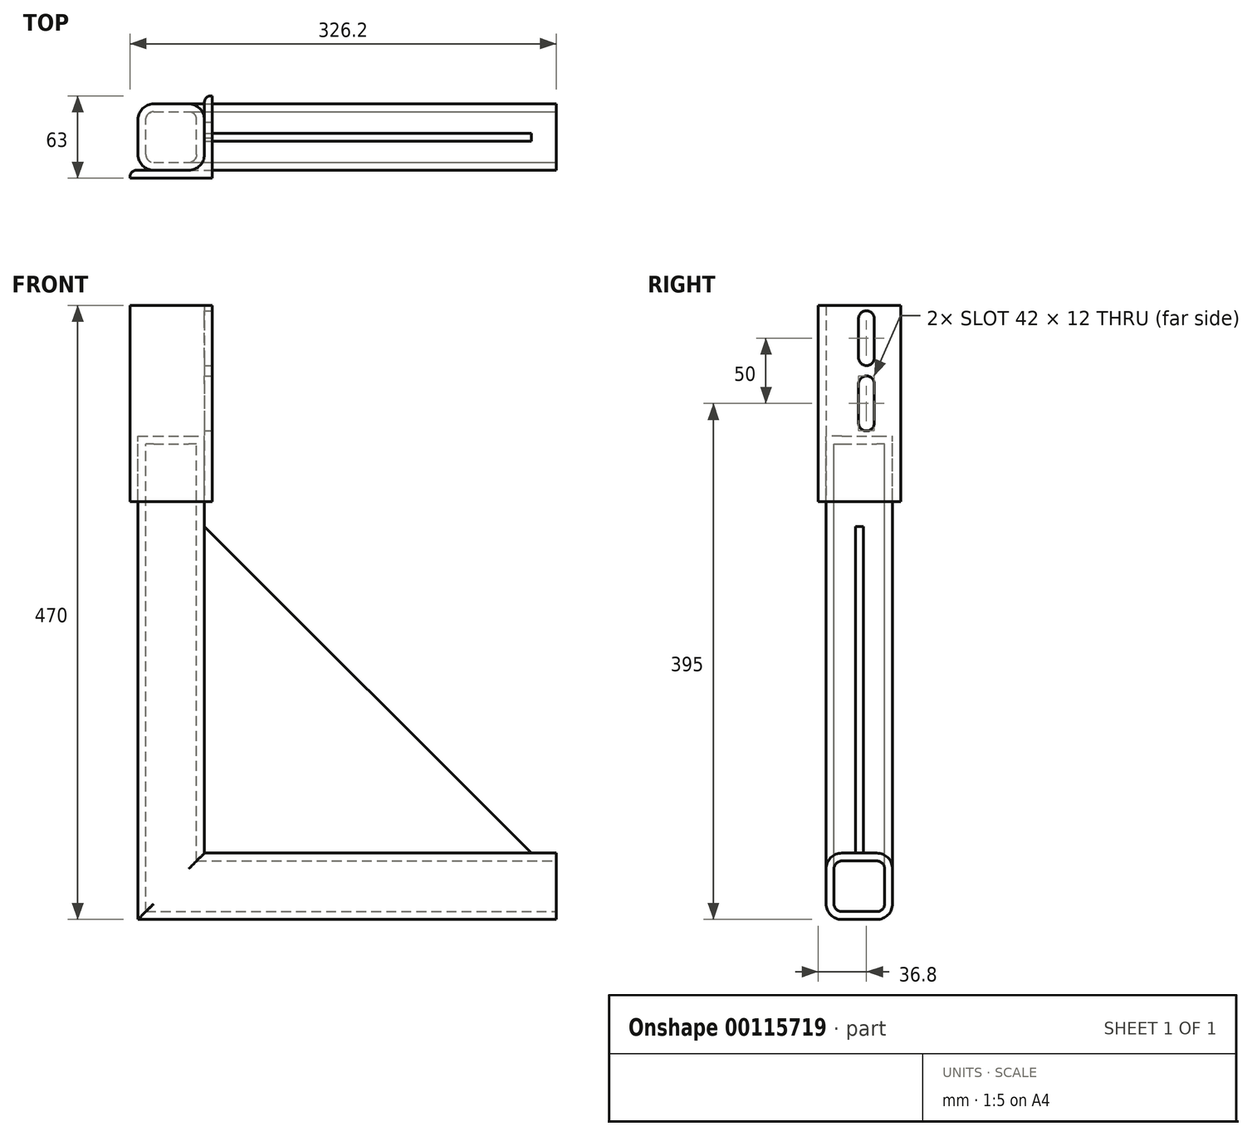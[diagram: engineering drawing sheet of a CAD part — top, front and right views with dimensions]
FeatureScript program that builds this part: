
annotation { "Feature Type Name" : "Feature", "Feature Type Description" : "" }
export const myFeature = defineFeature(function(context is Context, id is Id, definition is map)
    precondition{}
    {
        {
            var Q0;
            Q0=qCreatedBy(makeId("Front.planeOp"),FACE);
            var sketch = newSketch(context, id + "F0", { "sketchPlane" : qUnion([Q0])});
            skLineSegment(sketch, "E0.bottom", {"start": v(0, 0) * mm, "end": v(320, 0) * mm});
            skLineSegment(sketch, "E0.top", {"start": v(0, 370) * mm, "end": v(50.8, 370) * mm});
            skLineSegment(sketch, "E0.left", {"start": v(0, 0) * mm, "end": v(0, 370) * mm});
            skLineSegment(sketch, "E0.right", {"start": v(320, 0) * mm, "end": v(320, 50.8) * mm});
            skLineSegment(sketch, "E1.0", {"start": v(50.8, 50.8) * mm, "end": v(50.8, 370) * mm});
            skLineSegment(sketch, "E2.0", {"start": v(50.8, 50.8) * mm, "end": v(320, 50.8) * mm});
            skSolve(sketch);
        }
        {
            var Q0;
            Q0 = qSketchRegion(id + "F0", true);
            extrude(context, id + "F1", {"entities" : qUnion([Q0]), "endBound" : BoundingType.SYMMETRIC, "depth" : 50.8 * mm});
        }
        {
            var Q0;
            Q0=makeQuery(id+"F1.opExtrude","CAP_EDGE",EDGE,{"disambiguationData":[OSD([sQuery(id+"F0.wireOp",EDGE,"E1.0")])],"isStart":false});
            var Q1;
            Q1=makeQuery(id+"F1.opExtrude","CAP_EDGE",EDGE,{"disambiguationData":[OSD([sQuery(id+"F0.wireOp",EDGE,"E2.0")])],"isStart":false});
            var Q2;
            Q2=makeQuery(id+"F1.opExtrude","CAP_EDGE",EDGE,{"disambiguationData":[OSD([sQuery(id+"F0.wireOp",EDGE,"E2.0")])],"isStart":true});
            var Q3;
            Q3=makeQuery(id+"F1.opExtrude","CAP_EDGE",EDGE,{"disambiguationData":[OSD([sQuery(id+"F0.wireOp",EDGE,"E1.0")])],"isStart":true});
            var Q4;
            Q4=makeQuery(id+"F1.opExtrude","CAP_EDGE",EDGE,{"disambiguationData":[OSD([sQuery(id+"F0.wireOp",EDGE,"E0.bottom")])],"isStart":true});
            var Q5;
            Q5=makeQuery(id+"F1.opExtrude","CAP_EDGE",EDGE,{"disambiguationData":[OSD([sQuery(id+"F0.wireOp",EDGE,"E0.bottom")])],"isStart":false});
            var Q6;
            Q6=makeQuery(id+"F1.opExtrude","CAP_EDGE",EDGE,{"disambiguationData":[OSD([sQuery(id+"F0.wireOp",EDGE,"E0.left")])],"isStart":true});
            var Q7;
            Q7=makeQuery(id+"F1.opExtrude","CAP_EDGE",EDGE,{"disambiguationData":[OSD([sQuery(id+"F0.wireOp",EDGE,"E0.left")])],"isStart":false});
            fillet(context, id + "F2", {"entities" : qUnion([Q0, Q1, Q2, Q3, Q4, Q5, Q6, Q7]), "radius" : 12 * mm, "tangentPropagation" : true, "allowEdgeOverflow" : false});
        }
        {
            var Q0;
            Q0=makeQuery(id+"F1.opExtrude","SWEPT_FACE",FACE,{"disambiguationData":[OSD([sQuery(id+"F0.wireOp",EDGE,"E0.right")])]});
            shell(context, id + "F3", {"entities" : qUnion([Q0]), "thickness" : 6 * mm});
        }
        {
            var Q0;
            Q0=qCreatedBy(makeId("Front.planeOp"),FACE);
            var sketch = newSketch(context, id + "F4", { "sketchPlane" : qUnion([Q0])});
            skLineSegment(sketch, "E3.0", {"start": v(50.8, 50.8) * mm, "end": v(50.8, 370) * mm});
            skLineSegment(sketch, "E4.0", {"start": v(50.8, 50.8) * mm, "end": v(320, 50.8) * mm});
            skLineSegment(sketch, "E5.bottom", {"start": v(50.8, 50.8) * mm, "end": v(300.8, 50.8) * mm});
            skLineSegment(sketch, "E5.left", {"start": v(50.8, 50.8) * mm, "end": v(50.8, 300.8) * mm});
            skLineSegment(sketch, "E6", {"start": v(50.8, 300.8) * mm, "end": v(300.8, 50.8) * mm});
            skSolve(sketch);
        }
        {
            var Q0;
            Q0 = qSketchRegion(id + "F4", true);
            extrude(context, id + "F5", {"entities" : qUnion([Q0]), "operationType" : NewBodyOperationType.ADD, "endBound" : BoundingType.SYMMETRIC, "depth" : 6 * mm});
        }
        {
            var Q0;
            Q0=makeQuery(id+"F1.opExtrude","SWEPT_FACE",FACE,{"disambiguationData":[OSD([sQuery(id+"F0.wireOp",EDGE,"E0.top")])]});
            cPlane(context, id + "F6", {"entities" : qUnion([Q0]), "cplaneType" : CPlaneType.OFFSET, "offset" : 50 * mm, "oppositeDirection" : true, "width" : 150 * mm, "height" : 150 * mm});
        }
        {
            var Q0;
            Q0=qCreatedBy(id+"F6.planeOp",FACE);
            var sketch = newSketch(context, id + "F7", { "sketchPlane" : qUnion([Q0])});
            skLineSegment(sketch, "E7.0", {"start": v(12, -25.4) * mm, "end": v(50.8, -25.4) * mm, "construction": true});
            skLineSegment(sketch, "E8.0", {"start": v(50.8, -25.4) * mm, "end": v(50.8, 13.4) * mm, "construction": true});
            skPoint(sketch, "E9.orphan", {"position": v(38.8, -25.4) * mm});
            skPoint(sketch, "E10.orphan", {"position": v(50.8, -13.4) * mm});
            skLineSegment(sketch, "E11.bottom", {"start": v(38.8, -25.4) * mm, "end": v(-1.2, -25.4) * mm});
            skLineSegment(sketch, "E11.top", {"start": v(56.8, 31.6) * mm, "end": v(55.8, 31.6) * mm});
            skLineSegment(sketch, "E11.left", {"start": v(50.8, -13.4) * mm, "end": v(50.8, 26.6) * mm});
            skLineSegment(sketch, "E12.0", {"start": v(56.8, -31.4) * mm, "end": v(56.8, 31.6) * mm});
            skLineSegment(sketch, "E12.1", {"start": v(56.8, -31.4) * mm, "end": v(-6.2, -31.4) * mm});
            skLineSegment(sketch, "E13", {"start": v(-6.2, -30.4) * mm, "end": v(-6.2, -31.4) * mm});
            skPoint(sketch, "E14.visualSharp", {"position": v(50.8, -25.4) * mm});
            skArc(sketch, "E14.filletArc", {"start": v(38.8, -25.4) * mm, "mid": v(47.29, -21.89) * mm, "end": v(50.8, -13.4) * mm});
            skPoint(sketch, "E15.visualSharp", {"position": v(-6.2, -25.4) * mm});
            skArc(sketch, "E15.filletArc", {"start": v(-1.2, -25.4) * mm, "mid": v(-4.74, -26.86) * mm, "end": v(-6.2, -30.4) * mm});
            skPoint(sketch, "E16.visualSharp", {"position": v(50.8, 31.6) * mm});
            skArc(sketch, "E16.filletArc", {"start": v(55.8, 31.6) * mm, "mid": v(52.26, 30.14) * mm, "end": v(50.8, 26.6) * mm});
            skSolve(sketch);
        }
        {
            var Q0;
            Q0 = qSketchRegion(id + "F7", true);
            extrude(context, id + "F8", {"entities" : qUnion([Q0]), "depth" : 150 * mm});
        }
        {
            var Q0;
            Q0=makeQuery(id+"F8.opExtrude","SWEPT_FACE",FACE,{"disambiguationData":[OSD([sQuery(id+"F7.wireOp",EDGE,"E12.0")])]});
            var sketch = newSketch(context, id + "F9", { "sketchPlane" : qUnion([Q0])});
            skLineSegment(sketch, "E17.0", {"start": v(-31.4, 470) * mm, "end": v(31.6, 470) * mm, "construction": true});
            skLineSegment(sketch, "E18.0", {"start": v(-31.4, 420) * mm, "end": v(31.6, 420) * mm, "construction": true});
            skLineSegment(sketch, "E19.0", {"start": v(25.4, 470) * mm, "end": v(25.4, 38.8) * mm, "construction": true});
            skPoint(sketch, "E20.orphan", {"position": v(25.4, 370) * mm});
            skLineSegment(sketch, "E21.0", {"start": v(-31.4, 445) * mm, "end": v(31.6, 445) * mm, "construction": true});
            skLineSegment(sketch, "E22", {"start": v(5.4, 445) * mm, "end": v(5.4, 460) * mm});
            skLineSegment(sketch, "E23.MirrorCS", {"start": v(5.4, 445) * mm, "end": v(5.4, 430) * mm});
            skArc(sketch, "E24.0.endCap", {"start": v(-0.6, 460) * mm, "mid": v(5.4, 466) * mm, "end": v(11.4, 460) * mm});
            skLineSegment(sketch, "E24.0.left", {"start": v(-0.6, 445) * mm, "end": v(-0.6, 460) * mm});
            skLineSegment(sketch, "E24.0.right", {"start": v(11.4, 445) * mm, "end": v(11.4, 460) * mm});
            skArc(sketch, "E24.1.endCap", {"start": v(11.4, 430) * mm, "mid": v(5.4, 424) * mm, "end": v(-0.6, 430) * mm});
            skLineSegment(sketch, "E24.1.left", {"start": v(11.4, 445) * mm, "end": v(11.4, 430) * mm});
            skLineSegment(sketch, "E24.1.right", {"start": v(-0.6, 445) * mm, "end": v(-0.6, 430) * mm});
            skLineSegment(sketch, "E25.MirrorCS", {"start": v(-0.6, 395) * mm, "end": v(-0.6, 410) * mm});
            skLineSegment(sketch, "E26.MirrorCS", {"start": v(11.4, 395) * mm, "end": v(11.4, 410) * mm});
            skArc(sketch, "E27.MirrorCS", {"start": v(11.4, 410) * mm, "mid": v(5.4, 416) * mm, "end": v(-0.6, 410) * mm});
            skLineSegment(sketch, "E28.MirrorCS", {"start": v(11.4, 395) * mm, "end": v(11.4, 380) * mm});
            skLineSegment(sketch, "E29.MirrorCS", {"start": v(5.4, 395) * mm, "end": v(5.4, 410) * mm});
            skArc(sketch, "E30.MirrorCS", {"start": v(-0.6, 380) * mm, "mid": v(5.4, 374) * mm, "end": v(11.4, 380) * mm});
            skLineSegment(sketch, "E31.MirrorCS", {"start": v(-0.6, 395) * mm, "end": v(-0.6, 380) * mm});
            skLineSegment(sketch, "E32.MirrorCS", {"start": v(5.4, 395) * mm, "end": v(5.4, 380) * mm});
            skSolve(sketch);
        }
        {
            var Q0;
            Q0 = qSketchRegion(id + "F9", true);
            extrude(context, id + "F10", {"entities" : qUnion([Q0]), "operationType" : NewBodyOperationType.REMOVE, "endBound" : BoundingType.THROUGH_ALL, "oppositeDirection" : true, "depth" : 25 * mm});
        }
    });
